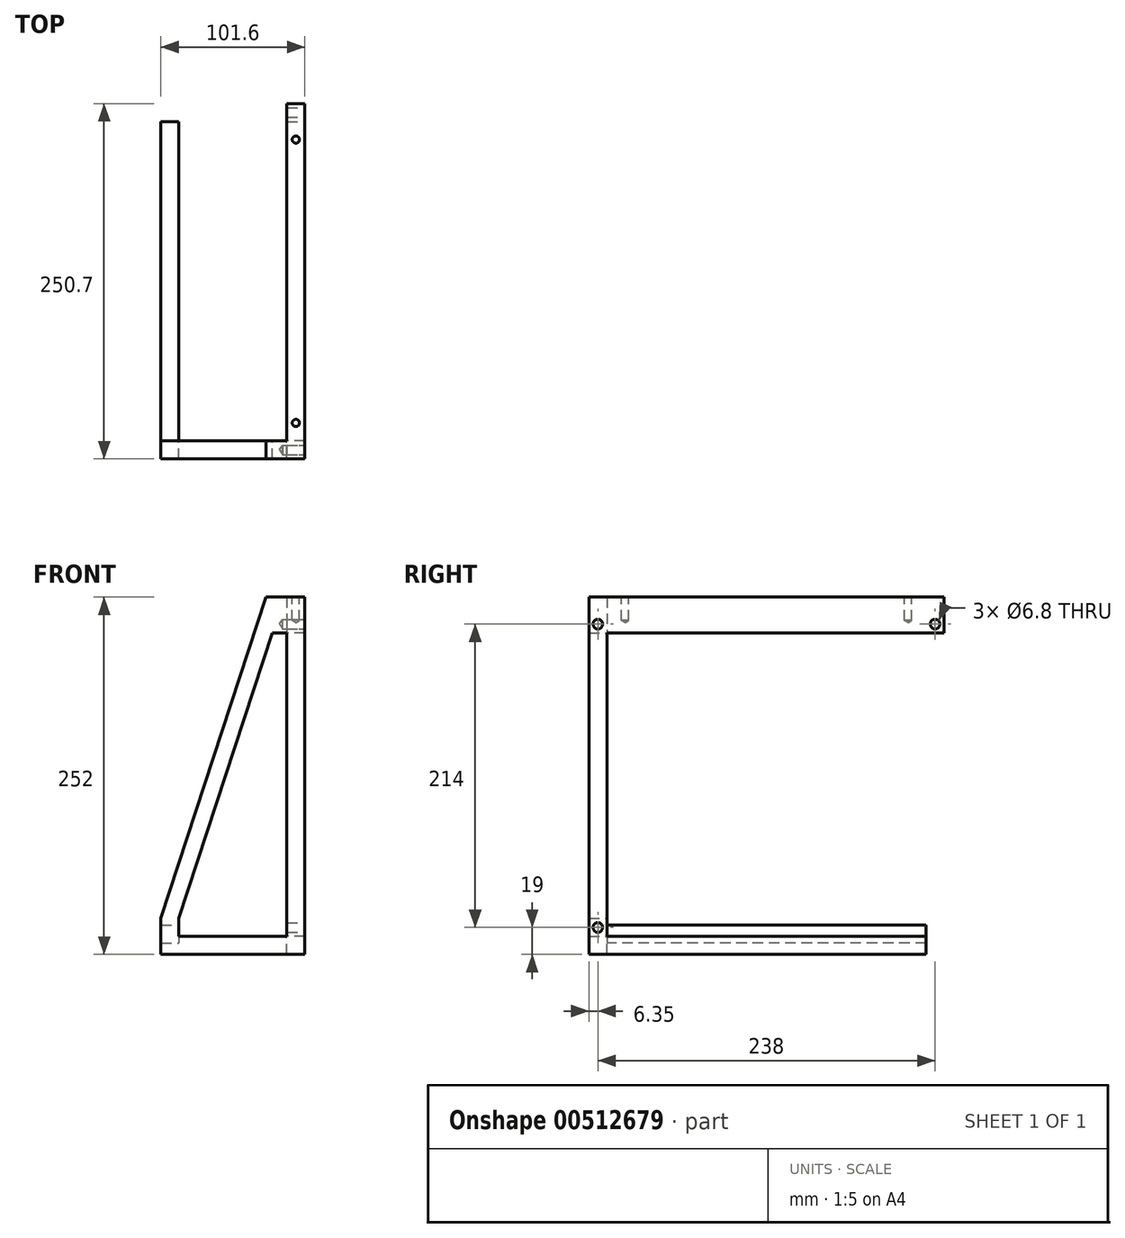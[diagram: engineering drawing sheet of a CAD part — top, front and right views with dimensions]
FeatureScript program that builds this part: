
annotation { "Feature Type Name" : "Feature", "Feature Type Description" : "" }
export const myFeature = defineFeature(function(context is Context, id is Id, definition is map)
    precondition{}
    {
        {
            var Q0;
            Q0=qCreatedBy(makeId("Front.planeOp"),FACE);
            var sketch = newSketch(context, id + "F0", { "sketchPlane" : qUnion([Q0])});
            skLineSegment(sketch, "E0", {"start": v(0, 0) * mm, "end": v(101.6, 0) * mm});
            skLineSegment(sketch, "E1", {"start": v(0, 0) * mm, "end": v(0, 25.4) * mm});
            skLineSegment(sketch, "E2", {"start": v(0, 25.4) * mm, "end": v(74.12, 252) * mm});
            skLineSegment(sketch, "E3", {"start": v(88.9, 12.7) * mm, "end": v(12.7, 12.7) * mm});
            skPoint(sketch, "E3.endSnap0", {"position": v(0, 12.7) * mm});
            skLineSegment(sketch, "E4", {"start": v(88.9, 226.6) * mm, "end": v(88.9, 12.7) * mm});
            skLineSegment(sketch, "E5", {"start": v(12.7, 25.4) * mm, "end": v(12.7, 12.7) * mm});
            skLineSegment(sketch, "E6", {"start": v(12.7, 25.4) * mm, "end": v(78.51, 226.6) * mm});
            skLineSegment(sketch, "E7", {"start": v(101.6, 0) * mm, "end": v(101.6, 252) * mm});
            skLineSegment(sketch, "E8", {"start": v(101.6, 252) * mm, "end": v(74.12, 252) * mm});
            skLineSegment(sketch, "E9", {"start": v(101.6, 252) * mm, "end": v(101.6, 239.3) * mm});
            skLineSegment(sketch, "E10", {"start": v(101.6, 239.3) * mm, "end": v(101.6, 226.6) * mm});
            skLineSegment(sketch, "E11", {"start": v(101.6, 226.6) * mm, "end": v(78.51, 226.6) * mm});
            skSolve(sketch);
        }
        {
            var Q0;
            Q0=makeQuery(id+"F0.imprint","IMPRINT",FACE,{"disambiguationData":[TD([[makeQuery(id+"F0.imprint","IMPRINT",EDGE,{"derivedFrom":sQuery(id+"F0.wireOp",EDGE,"E0")}),1.0]])]});
            extrude(context, id + "F1", {"entities" : qUnion([Q0]), "depth" : 12.7 * mm});
        }
        {
            var Q0;
            Q0=makeQuery(id+"F1.opExtrude","CAP_FACE",FACE,{"disambiguationData":[OSD([sQuery(id+"F0.wireOp",EDGE,"E0"),sQuery(id+"F0.wireOp",EDGE,"E1"),sQuery(id+"F0.wireOp",EDGE,"E2"),sQuery(id+"F0.wireOp",EDGE,"E3"),sQuery(id+"F0.wireOp",EDGE,"E4"),sQuery(id+"F0.wireOp",EDGE,"E5"),sQuery(id+"F0.wireOp",EDGE,"E6"),sQuery(id+"F0.wireOp",EDGE,"E7"),sQuery(id+"F0.wireOp",EDGE,"E8"),sQuery(id+"F0.wireOp",EDGE,"E9"),sQuery(id+"F0.wireOp",EDGE,"ifux6GjV-N4uH-BMXz-Fh14-0Awf5LUvRzG1")])],"isStart":true});
            var sketch = newSketch(context, id + "F2", { "sketchPlane" : qUnion([Q0])});
            skLineSegment(sketch, "E12.bottom", {"start": v(-101.6, 0) * mm, "end": v(-88.9, 0) * mm});
            skLineSegment(sketch, "E12.top", {"start": v(-101.6, 12.7) * mm, "end": v(-88.9, 12.7) * mm});
            skLineSegment(sketch, "E12.left", {"start": v(-101.6, 0) * mm, "end": v(-101.6, 12.7) * mm});
            skLineSegment(sketch, "E12.right", {"start": v(-88.9, 0) * mm, "end": v(-88.9, 12.7) * mm});
            skLineSegment(sketch, "E13.bottom", {"start": v(-101.6, 252) * mm, "end": v(-88.9, 252) * mm});
            skLineSegment(sketch, "E13.left", {"start": v(-101.6, 252) * mm, "end": v(-101.6, 226.6) * mm});
            skLineSegment(sketch, "E13.right", {"start": v(-88.9, 252) * mm, "end": v(-88.9, 12.7) * mm});
            skLineSegment(sketch, "E14", {"start": v(0, 0) * mm, "end": v(0, 7.87) * mm});
            skLineSegment(sketch, "E15.bottom", {"start": v(0, 7.87) * mm, "end": v(-12.7, 7.87) * mm});
            skLineSegment(sketch, "E15.top", {"start": v(0, 20.57) * mm, "end": v(-12.7, 20.57) * mm});
            skLineSegment(sketch, "E15.left", {"start": v(0, 7.87) * mm, "end": v(0, 20.57) * mm});
            skLineSegment(sketch, "E15.right", {"start": v(-12.7, 7.87) * mm, "end": v(-12.7, 20.57) * mm});
            skLineSegment(sketch, "E16", {"start": v(-88.9, 12.7) * mm, "end": v(-88.9, 229.16) * mm});
            skLineSegment(sketch, "E17", {"start": v(-101.6, 226.6) * mm, "end": v(-88.9, 226.6) * mm});
            skLineSegment(sketch, "E18", {"start": v(-88.9, 226.6) * mm, "end": v(-88.9, 229.16) * mm});
            skSolve(sketch);
        }
        {
            var Q0;
            Q0=makeQuery(id+"F2.imprint","IMPRINT",FACE,{"disambiguationData":[TD([[makeQuery(id+"F2.imprint","IMPRINT",EDGE,{"derivedFrom":sQuery(id+"F2.wireOp",EDGE,"E12.bottom")}),-1.0]])]});
            var Q1;
            Q1=makeQuery(id+"F2.imprint","IMPRINT",FACE,{"disambiguationData":[TD([[makeQuery(id+"F2.imprint","IMPRINT",EDGE,{"derivedFrom":sQuery(id+"F2.wireOp",EDGE,"IoMlpHq2-cJgv-B8ZE-quO5-kUIREItqClHN.bottom")}),-1.0]])]});
            var Q2;
            Q2=makeQuery(id+"F2.imprint","IMPRINT",FACE,{"disambiguationData":[TD([[makeQuery(id+"F2.imprint","IMPRINT",EDGE,{"derivedFrom":sQuery(id+"F2.wireOp",EDGE,"E13.bottom")}),-1.0]])]});
            var Q3;
            {var subQ2=sQuery(id+"F2.wireOp",EDGE,"E15.bottom");Q3=makeQuery(id+"F2.imprint","IMPRINT",FACE,{"disambiguationData":[TD([[makeQuery(id+"F2.imprint","IMPRINT",EDGE,{"derivedFrom":subQ2}),-1.0]])]});}
            extrude(context, id + "F3", {"entities" : qUnion([Q0, Q1, Q2, Q3]), "operationType" : NewBodyOperationType.ADD, "depth" : 225.3 * mm});
        }
        {
            var Q0;
            Q0=makeQuery(id+"F3.opExtrude","CAP_FACE",FACE,{"disambiguationData":[OSD([sQuery(id+"F2.wireOp",EDGE,"E13.bottom"),sQuery(id+"F2.wireOp",EDGE,"E13.top"),sQuery(id+"F2.wireOp",EDGE,"E13.left"),sQuery(id+"F2.wireOp",EDGE,"E13.right")])],"isStart":false});
            var sketch = newSketch(context, id + "F4", { "sketchPlane" : qUnion([Q0])});
            skLineSegment(sketch, "E19.0", {"start": v(0, 25.4) * mm, "end": v(-74.12, 252) * mm});
            skLineSegment(sketch, "E19.1.0", {"start": v(-101.6, 0) * mm, "end": v(-101.6, 252) * mm});
            skLineSegment(sketch, "E19.1.1", {"start": v(-101.6, 252) * mm, "end": v(-74.12, 252) * mm});
            skLineSegment(sketch, "E19.1.2", {"start": v(-74.12, 252) * mm, "end": v(0, 25.4) * mm});
            skLineSegment(sketch, "E19.1.3", {"start": v(0, 25.4) * mm, "end": v(0, 0) * mm});
            skLineSegment(sketch, "E19.1.4", {"start": v(0, 0) * mm, "end": v(-101.6, 0) * mm});
            skLineSegment(sketch, "E20.0", {"start": v(-12.7, 25.4) * mm, "end": v(-12.7, 25.4) * mm});
            skLineSegment(sketch, "E20.2", {"start": v(-88.9, 25.4) * mm, "end": v(-88.9, 12.7) * mm});
            skLineSegment(sketch, "E20.3", {"start": v(-12.7, 25.4) * mm, "end": v(-12.7, 12.7) * mm});
            skLineSegment(sketch, "E20.4", {"start": v(-88.9, 12.7) * mm, "end": v(-12.7, 12.7) * mm});
            skLineSegment(sketch, "E21.0", {"start": v(-88.9, 226.6) * mm, "end": v(-78.51, 226.6) * mm});
            skLineSegment(sketch, "E21.1", {"start": v(-12.7, 25.4) * mm, "end": v(-78.51, 226.6) * mm});
            skLineSegment(sketch, "E21.2", {"start": v(-88.9, 226.6) * mm, "end": v(-88.9, 12.7) * mm});
            skLineSegment(sketch, "E21.3", {"start": v(-88.9, 226.6) * mm, "end": v(-88.9, 25.4) * mm});
            skSolve(sketch);
        }
        {
            var Q0;
            {var subQ9=sQuery(id+"F4.wireOp",EDGE,"E19.1.2");Q0=makeQuery(id+"F4.imprint","IMPRINT",FACE,{"disambiguationData":[TD([[makeQuery(id+"F4.imprint","IMPRINT",EDGE,{"derivedFrom":subQ9}),-1.0]])]});}
            var Q1;
            {var subQ7=makeQuery(id+"F3.opExtrude","CAP_EDGE",EDGE,{"disambiguationData":[OSD([sQuery(id+"F2.wireOp",EDGE,"w5KUmTXB-0kq7-Mjd3-9YYb-6JzhaBfLAejB")])],"isStart":false});Q1=makeQuery(id+"F4.imprint","IMPRINT",FACE,{"disambiguationData":[TD([[makeQuery(id+"F4.imprint","IMPRINT",EDGE,{"derivedFrom":subQ7}),1.0]])]});}
            var Q2;
            {var subQ3=makeQuery(id+"F3.opExtrude","CAP_EDGE",EDGE,{"disambiguationData":[OSD([sQuery(id+"F2.wireOp",EDGE,"E17")])],"isStart":false});Q2=makeQuery(id+"F4.imprint","IMPRINT",FACE,{"disambiguationData":[TD([[makeQuery(id+"F4.imprint","IMPRINT",EDGE,{"derivedFrom":subQ3}),1.0]])]});}
            extrude(context, id + "F5", {"entities" : qUnion([Q0, Q1, Q2]), "operationType" : NewBodyOperationType.ADD, "depth" : 12.7 * mm});
        }
        {
            var Q0;
            Q0=makeQuery(id+"F5.boolean.opBoolean","MERGE",FACE,{"derivedFrom":[makeQuery(id+"F3.boolean.opBoolean","MERGE",FACE,{"derivedFrom":[makeQuery(id+"F1.opExtrude","SWEPT_FACE",FACE,{"disambiguationData":[OSD([sQuery(id+"F0.wireOp",EDGE,"E7"),sQuery(id+"F0.wireOp",EDGE,"E9")])]}),makeQuery(id+"F3.opExtrude","SWEPT_FACE",FACE,{"disambiguationData":[OSD([sQuery(id+"F2.wireOp",EDGE,"E12.left")])]}),makeQuery(id+"F3.opExtrude","SWEPT_FACE",FACE,{"disambiguationData":[OSD([sQuery(id+"F2.wireOp",EDGE,"E13.left")])]})]}),makeQuery(id+"F5.opExtrude","SWEPT_FACE",FACE,{"disambiguationData":[OSD([sQuery(id+"F4.wireOp",EDGE,"E19.1.0")])]})]});
            var sketch = newSketch(context, id + "F6", { "sketchPlane" : qUnion([Q0])});
            skLineSegment(sketch, "E22", {"start": v(-12.7, 0) * mm, "end": v(-6.35, 0) * mm});
            skLineSegment(sketch, "E23", {"start": v(-6.35, 0) * mm, "end": v(-6.35, 19) * mm});
            skPoint(sketch, "E24.endSnap0", {"position": v(0, 119.65) * mm});
            skLineSegment(sketch, "E25", {"start": v(-6.35, 19) * mm, "end": v(-6.35, 233) * mm});
            skLineSegment(sketch, "E26", {"start": v(112.65, 12.7) * mm, "end": v(112.65, 83.29) * mm});
            skLineSegment(sketch, "E27.MirrorCS", {"start": v(231.65, 19) * mm, "end": v(231.65, 233) * mm});
            skSolve(sketch);
        }
        {
            var Q0;
            Q0=sQuery(id+"F6.wireOp",VERTEX,"301810f4-b5b0-48fe-9fed-440b1d064d410.MirrorCS.end");
            var Q1;
            Q1=sQuery(id+"F6.wireOp",VERTEX,"60cd97af-2dfd-4b1e-9da8-f66463ed67490.MirrorCS.end");
            var Q2;
            Q2=sQuery(id+"F6.wireOp",VERTEX,"E23.end");
            var Q3;
            Q3=sQuery(id+"F6.wireOp",VERTEX,"c38dfc3b-03b4-4e9e-9462-be59b06b3c6f0.MirrorCS.end");
            var Q4;
            Q4=sQuery(id+"F6.wireOp",VERTEX,"E25.end");
            var Q5;
            Q5=sQuery(id+"F6.wireOp",VERTEX,"E27.MirrorCS.end");
            var Q6;
            Q6=sQuery(id+"F6.wireOp",VERTEX,"E27.MirrorCS.start");
            var Q7;
            Q7=makeQuery(id+"F1.opExtrude","SWEPT_BODY",BODY,{"disambiguationData":[OSD([sQuery(id+"F0.wireOp",EDGE,"E0"),sQuery(id+"F0.wireOp",EDGE,"E1"),sQuery(id+"F0.wireOp",EDGE,"E2"),sQuery(id+"F0.wireOp",EDGE,"E3"),sQuery(id+"F0.wireOp",EDGE,"E4"),sQuery(id+"F0.wireOp",EDGE,"E5"),sQuery(id+"F0.wireOp",EDGE,"E6"),sQuery(id+"F0.wireOp",EDGE,"E7"),sQuery(id+"F0.wireOp",EDGE,"E8"),sQuery(id+"F0.wireOp",EDGE,"E9"),sQuery(id+"F0.wireOp",EDGE,"ifux6GjV-N4uH-BMXz-Fh14-0Awf5LUvRzG1")])]});
            hole(context, id + "F7", {"style" : HoleStyle.SIMPLE, "endStyle" : HoleEndStyle.BLIND, "standardTappedOrClearance" : lookupTablePath({ "standard" : "ISO", "engagement" : "75%", "pitch" : "1.25 mm", "size" : "M8", "type" : "Tapped" }), "standardBlindInLast" : lookupTablePath({ "standard" : "ISO", "engagement" : "75%", "pitch" : "1.25 mm", "size" : "M8", "type" : "Tapped" }), "holeDiameter" : 6.8 * mm, "showTappedDepth" : true, "holeDepth" : 15.75 * mm, "isTappedThrough" : true, "tappedDepth" : 12 * mm, "tapClearance" : 3, "startFromSketch" : true, "locations" : qUnion([Q0, Q1, Q2, Q3, Q4, Q5, Q6]), "scope" : qUnion([Q7]), "majorDiameter" : 8 * mm});
        }
        {
            var Q0;
            Q0=makeQuery(id+"F5.boolean.opBoolean","MERGE",FACE,{"derivedFrom":[makeQuery(id+"F3.boolean.opBoolean","MERGE",FACE,{"derivedFrom":[makeQuery(id+"F1.opExtrude","SWEPT_FACE",FACE,{"disambiguationData":[OSD([sQuery(id+"F0.wireOp",EDGE,"E8")])]}),makeQuery(id+"F3.opExtrude","SWEPT_FACE",FACE,{"disambiguationData":[OSD([sQuery(id+"F2.wireOp",EDGE,"E13.bottom")])]})]}),makeQuery(id+"F5.opExtrude","SWEPT_FACE",FACE,{"disambiguationData":[OSD([sQuery(id+"F4.wireOp",EDGE,"E19.1.1")])]})]});
            var sketch = newSketch(context, id + "F8", { "sketchPlane" : qUnion([Q0])});
            skLineSegment(sketch, "E28", {"start": v(101.6, 238) * mm, "end": v(95.25, 238) * mm});
            skLineSegment(sketch, "E29", {"start": v(95.25, 238) * mm, "end": v(95.25, 212.6) * mm});
            skLineSegment(sketch, "E30", {"start": v(101.6, 112.65) * mm, "end": v(74.15, 112.65) * mm});
            skLineSegment(sketch, "E31.MirrorCS", {"start": v(95.25, -12.7) * mm, "end": v(95.25, 12.7) * mm});
            skSolve(sketch);
        }
        {
            var Q0;
            Q0=sQuery(id+"F8.wireOp",VERTEX,"E29.end");
            var Q1;
            Q1=sQuery(id+"F8.wireOp",VERTEX,"E31.MirrorCS.end");
            var Q2;
            Q2=makeQuery(id+"F1.opExtrude","SWEPT_BODY",BODY,{"disambiguationData":[OSD([sQuery(id+"F0.wireOp",EDGE,"E0"),sQuery(id+"F0.wireOp",EDGE,"E1"),sQuery(id+"F0.wireOp",EDGE,"E2"),sQuery(id+"F0.wireOp",EDGE,"E3"),sQuery(id+"F0.wireOp",EDGE,"E4"),sQuery(id+"F0.wireOp",EDGE,"E5"),sQuery(id+"F0.wireOp",EDGE,"E6"),sQuery(id+"F0.wireOp",EDGE,"E7"),sQuery(id+"F0.wireOp",EDGE,"E8"),sQuery(id+"F0.wireOp",EDGE,"E9"),sQuery(id+"F0.wireOp",EDGE,"ifux6GjV-N4uH-BMXz-Fh14-0Awf5LUvRzG1")])]});
            hole(context, id + "F9", {"style" : HoleStyle.SIMPLE, "endStyle" : HoleEndStyle.BLIND, "standardTappedOrClearance" : lookupTablePath({ "standard" : "ANSI", "engagement" : "75%", "pitch" : "20 tpi", "size" : "1/4", "type" : "Tapped" }), "standardBlindInLast" : lookupTablePath({ "standard" : "ANSI", "engagement" : "75%", "pitch" : "20 tpi", "size" : "1/4", "type" : "Tapped" }), "holeDiameter" : 5.1 * mm, "showTappedDepth" : true, "holeDepth" : 16.51 * mm, "isTappedThrough" : true, "tappedDepth" : 12.7 * mm, "tapClearance" : 3, "locations" : qUnion([Q0, Q1]), "scope" : qUnion([Q2]), "majorDiameter" : 6.35 * mm});
        }
    });
